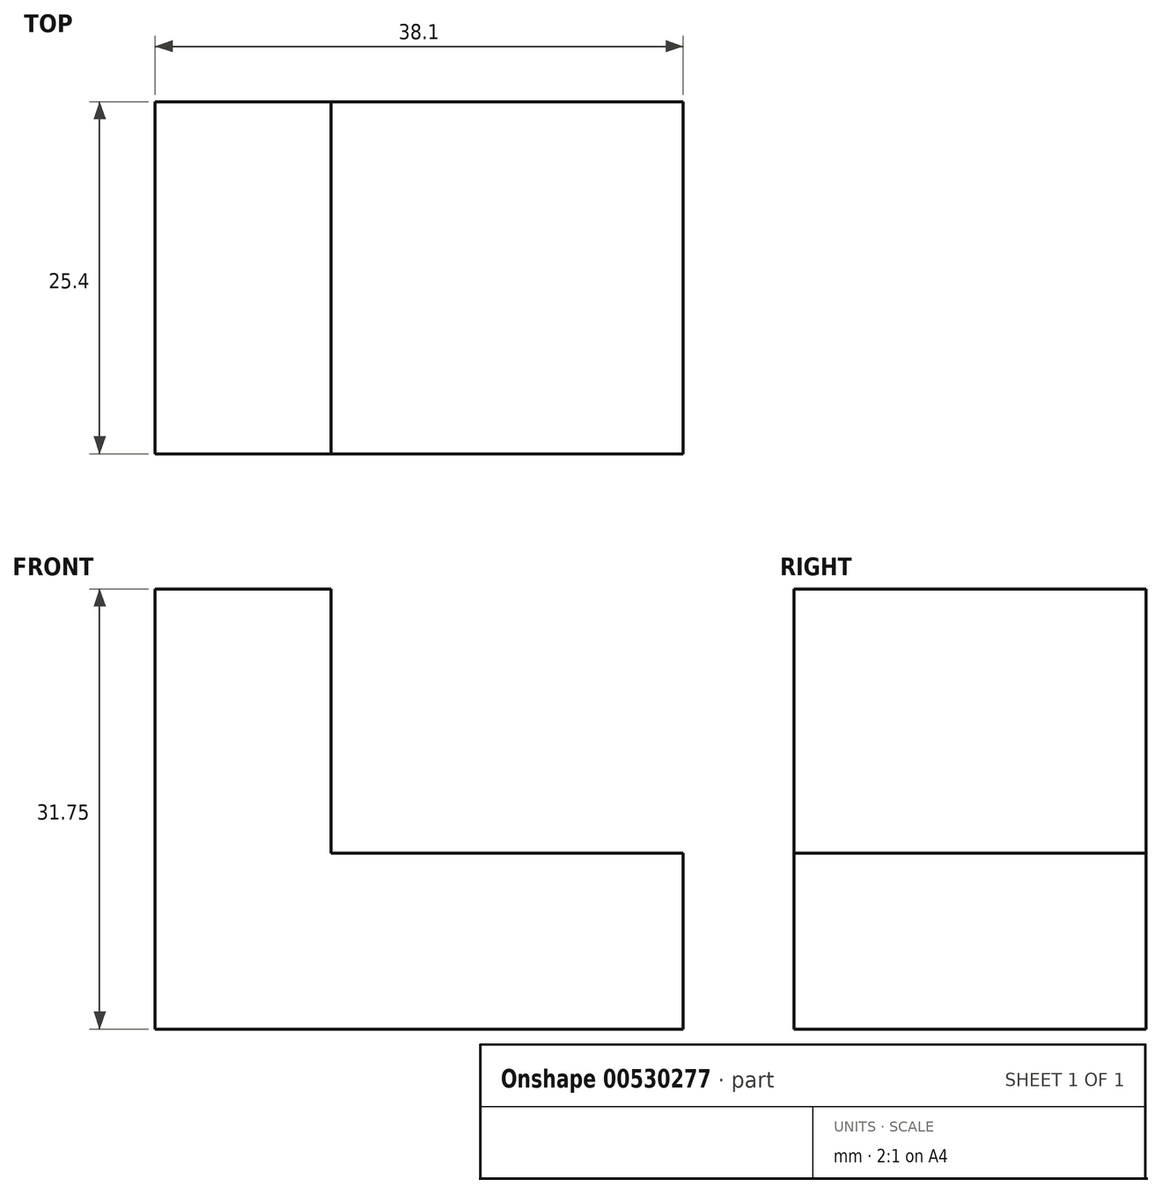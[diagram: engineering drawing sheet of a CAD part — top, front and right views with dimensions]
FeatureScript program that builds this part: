
annotation { "Feature Type Name" : "Feature", "Feature Type Description" : "" }
export const myFeature = defineFeature(function(context is Context, id is Id, definition is map)
    precondition{}
    {
        {
            var Q0;
            Q0=qCreatedBy(makeId("Front.planeOp"),FACE);
            var sketch = newSketch(context, id + "F0", { "sketchPlane" : qUnion([Q0])});
            skLineSegment(sketch, "E0", {"start": v(-50.8, 31.75) * mm, "end": v(-50.8, 0) * mm});
            skLineSegment(sketch, "E1", {"start": v(-50.8, 0) * mm, "end": v(-12.7, 0) * mm});
            skLineSegment(sketch, "E2", {"start": v(-12.7, 0) * mm, "end": v(-12.7, 12.7) * mm});
            skLineSegment(sketch, "E3", {"start": v(-12.7, 12.7) * mm, "end": v(-38.1, 12.7) * mm});
            skLineSegment(sketch, "E4", {"start": v(-38.1, 12.7) * mm, "end": v(-38.1, 31.75) * mm});
            skLineSegment(sketch, "E5", {"start": v(-38.1, 31.75) * mm, "end": v(-50.8, 31.75) * mm});
            skSolve(sketch);
        }
        {
            var Q0;
            Q0=makeQuery(id+"F0.imprint","IMPRINT",FACE,{"disambiguationData":[TD([[makeQuery(id+"F0.imprint","IMPRINT",EDGE,{"derivedFrom":sQuery(id+"F0.wireOp",EDGE,"E0")}),1.0]])]});
            extrude(context, id + "F1", {"entities" : qUnion([Q0]), "depth" : 25.4 * mm, "offsetDistance" : 25.4 * mm});
        }
    });
